# Revit family: Detector-DETECT-X_-P.v2
name_source: partatom
category: Equipos especializados
revit_build: Autodesk Revit 2018 (Build: 20170927_1515(x64)
units: mm (PartAtom-declared; Revit-internal decimal feet)

## family parameters
Anfitrión = Cara
Compartido = No
Corte con vacíos al cargar = No
Cota de conector redondo = Diámetro de uso
Punto de cálculo de habitación = No
Tipo de pieza = Normal

## types (2) — shared parameters
Cable section = 0.15mm² to 1 mm² (Zennio device inputs specification. Look up compatible devices)
Connection type = Screw terminal clamp
Consumption (detecting status) = 1mA
Consumption (stand-by) = 15μA
Degree of protection = IP 20, clean environment
Depth = 17 mm
Elevación por defecto = 1219 mm
External power supply = Provide by the external device through the common terminal
Fabricante = Zennio Avance y Tecnología, S.L.
Housing material = PC/ABS FR V0 halogen free - Silver
Internal_radius = 18 mm
Lens material = PE-HD_lens
Lens_radius = 10 mm  [stored 0.0328084 ft]
Max cable length = 30 meters (Zennio device inputs specification. Look up compatible devices)
Operating temperature = 0ºC to +55ºC
PCB CTI index = 175 V
Product Page URL = http://www.zennio.com
Radius = 25 mm  [stored 0.082021 ft]
Storage temperature = -20ºC to +70ºC
URL = http://www.zennio.com
Weight = 25g
Width = 3 mm  [stored 0.00984252 ft]

## per-type parameters (varying)
| type | Constraints | Descripción | Detection angle axe X | Detection angle axe Y | Detection_distance_X_Height_2.7m | Detection_distance_X_Height_5m | Detection_distance_Y_Height_2.7m | Detection_distance_Y_Height_5m | Luminosity range | Operating humidity | Storage humidity |
| ZN1IO-DETECT-X | 1 | Motion detector | 51.00° | 46.00° | 6670 mm  [stored 21.8832 ft] | 12350 mm | 5590 mm  [stored 18.3399 ft] | 10360 mm | Not available | 30 to 85% RH (no condensation) | 30 to 85% RH (no condensation) |
| ZN1IO-DETECT-P | 0 | Motion detector with luminosity sensor | 51.30° | 46.30° | 7450 mm  [stored 24.4423 ft] | 13800 mm  [stored 45.2756 ft] | 6260 mm  [stored 20.5381 ft] | 11600 mm  [stored 38.0577 ft] | TBD | 3 to 95% RH (no condensation) | 3 to 95% RH (no condensation) |

note: column(s) folded — value = type name in every type: Modelo

note: [stored X ft] marks values corroborated as IEEE doubles in the binary element streams (Revit-internal decimal feet)
